annotation { "Feature Type Name" : "Feature", "Feature Type Description" : "" }
export const myFeature = defineFeature(function(context is Context, id is Id, definition is map)
    precondition{}
    {
        {
            var Q0;
            Q0=qCreatedBy(makeId("Top.planeOp"),FACE);
            var sketch = newSketch(context, id + "F0", { "sketchPlane" : qUnion([Q0])});
            skLineSegment(sketch, "E0.bottom", {"start": v(40, 27) * mm, "end": v(-40, 27) * mm});
            skLineSegment(sketch, "E0.top", {"start": v(40, -27) * mm, "end": v(-40, -27) * mm});
            skLineSegment(sketch, "E0.left", {"start": v(43, 24) * mm, "end": v(43, -24) * mm});
            skLineSegment(sketch, "E0.right", {"start": v(-43, 24) * mm, "end": v(-43, -24) * mm});
            skPoint(sketch, "E0.middle", {"position": v(0, 0) * mm});
            skPoint(sketch, "E1.visualSharp", {"position": v(-43, 27) * mm});
            skArc(sketch, "E1.filletArc", {"start": v(-40, 27) * mm, "mid": v(-42.12, 26.12) * mm, "end": v(-43, 24) * mm});
            skPoint(sketch, "E2.visualSharp", {"position": v(43, 27) * mm});
            skArc(sketch, "E2.filletArc", {"start": v(43, 24) * mm, "mid": v(42.12, 26.12) * mm, "end": v(40, 27) * mm});
            skPoint(sketch, "E3.visualSharp", {"position": v(43, -27) * mm});
            skArc(sketch, "E3.filletArc", {"start": v(40, -27) * mm, "mid": v(42.12, -26.12) * mm, "end": v(43, -24) * mm});
            skPoint(sketch, "E4.visualSharp", {"position": v(-43, -27) * mm});
            skArc(sketch, "E4.filletArc", {"start": v(-43, -24) * mm, "mid": v(-42.12, -26.12) * mm, "end": v(-40, -27) * mm});
            skSolve(sketch);
        }
        {
            var Q0;
            Q0=makeQuery(id+"F0.imprint","IMPRINT",FACE,{"disambiguationData":[TD([[makeQuery(id+"F0.imprint","IMPRINT",EDGE,{"derivedFrom":sQuery(id+"F0.wireOp",EDGE,"E0.bottom")}),1.0]])]});
            extrude(context, id + "F1", {"entities" : qUnion([Q0]), "depth" : 4 * mm});
        }
        {
            var Q0;
            Q0=makeQuery(id+"F1.opExtrude","CAP_FACE",FACE,{"disambiguationData":[OSD([sQuery(id+"F0.wireOp",EDGE,"E0.bottom"),sQuery(id+"F0.wireOp",EDGE,"E0.top"),sQuery(id+"F0.wireOp",EDGE,"E0.left"),sQuery(id+"F0.wireOp",EDGE,"E0.right"),sQuery(id+"F0.wireOp",EDGE,"E1.filletArc"),sQuery(id+"F0.wireOp",EDGE,"E2.filletArc"),sQuery(id+"F0.wireOp",EDGE,"E3.filletArc"),sQuery(id+"F0.wireOp",EDGE,"E4.filletArc")])],"isStart":false});
            var sketch = newSketch(context, id + "F2", { "sketchPlane" : qUnion([Q0])});
            skLineSegment(sketch, "E5.bottom", {"start": v(40, 24) * mm, "end": v(-40, 24) * mm, "construction": true});
            skLineSegment(sketch, "E5.top", {"start": v(40, -24) * mm, "end": v(-40, -24) * mm, "construction": true});
            skLineSegment(sketch, "E5.left", {"start": v(40, 24) * mm, "end": v(40, -24) * mm, "construction": true});
            skLineSegment(sketch, "E5.right", {"start": v(-40, 24) * mm, "end": v(-40, -24) * mm, "construction": true});
            skPoint(sketch, "E5.middle", {"position": v(0, 0) * mm});
            skText(sketch, "E6", { "text": "Good For One (1)", "fontName": "OpenSans-Regular.ttf"});
            const initialGuessF2  = {"E6": [-0.04, 0.0168, 1, 0, 0.0072]};
            skSetInitialGuess(sketch, initialGuessF2);
            skSolve(sketch);
        }
        {
            var Q0;
            Q0 = qSketchRegion(id + "F2", true);
            extrude(context, id + "F3", {"entities" : qUnion([Q0]), "operationType" : NewBodyOperationType.REMOVE, "oppositeDirection" : true, "depth" : 2 * mm});
        }
        {
            var Q0;
            {var subQ0=sQuery(id+"F0.wireOp",EDGE,"E0.top");var subQ1=sQuery(id+"F0.wireOp",EDGE,"E0.right");var subQ2=sQuery(id+"F0.wireOp",EDGE,"E0.bottom");var subQ3=sQuery(id+"F0.wireOp",EDGE,"E1.filletArc");var subQ4=sQuery(id+"F0.wireOp",EDGE,"E2.filletArc");var subQ5=sQuery(id+"F0.wireOp",EDGE,"E3.filletArc");var subQ6=sQuery(id+"F0.wireOp",EDGE,"E4.filletArc");var subQ7=sQuery(id+"F0.wireOp",EDGE,"E0.left");Q0=makeQuery(id+"F3.boolean.opBoolean","SPLIT",FACE,{"disambiguationData":[TD([makeQuery(id+"F1.opExtrude","SWEPT_FACE",FACE,{"disambiguationData":[OSD([subQ2])]})])],"derivedFrom":makeQuery(id+"F1.opExtrude","CAP_FACE",FACE,{"disambiguationData":[OSD([subQ2,subQ0,subQ7,subQ1,subQ3,subQ4,subQ5,subQ6])],"isStart":false})});}
            var sketch = newSketch(context, id + "F4", { "sketchPlane" : qUnion([Q0])});
            skPoint(sketch, "E7.endSnap0", {"position": v(0, -27) * mm});
            skText(sketch, "E8", { "text": "Hubby Cooks", "fontName": "OpenSans-Regular.ttf"});
            skText(sketch, "E9", { "text": "Dinner Night", "fontName": "OpenSans-Regular.ttf"});
            const initialGuessF4  = {"E8": [-0.03305, 0, 1, 0, 0.00767], "E9": [-0.03637, -0.01224, 1, 0, 0.00876]};
            skSetInitialGuess(sketch, initialGuessF4);
            skSolve(sketch);
        }
        {
            var Q0;
            Q0 = qSketchRegion(id + "F4", true);
            extrude(context, id + "F5", {"entities" : qUnion([Q0]), "operationType" : NewBodyOperationType.REMOVE, "oppositeDirection" : true, "depth" : 2 * mm});
        }
    });